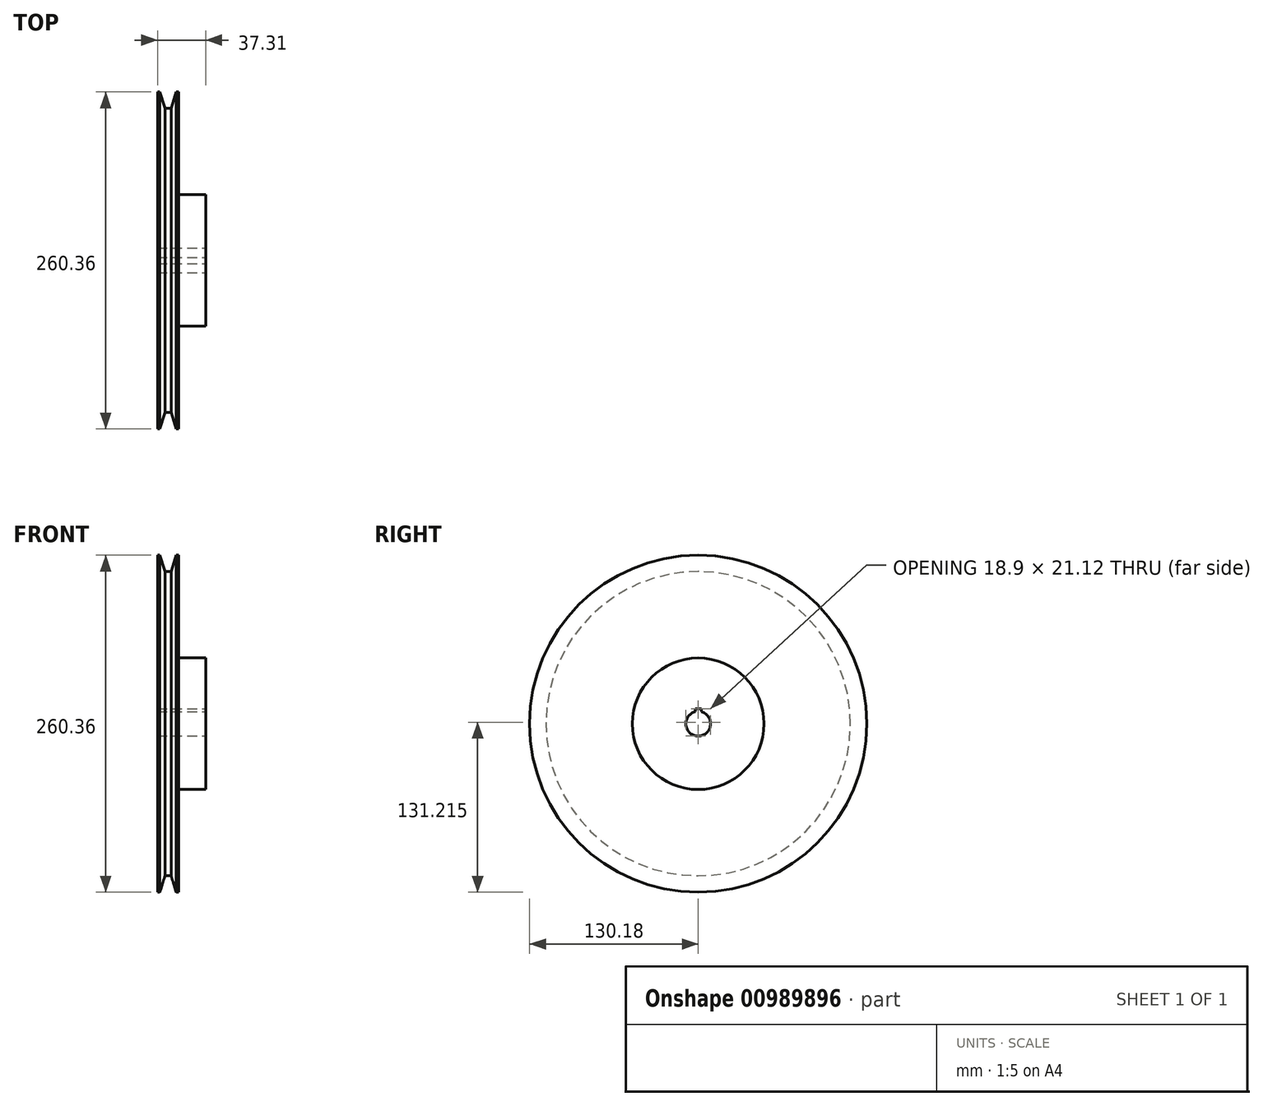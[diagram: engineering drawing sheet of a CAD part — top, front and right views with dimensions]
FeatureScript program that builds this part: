
annotation { "Feature Type Name" : "Feature", "Feature Type Description" : "" }
export const myFeature = defineFeature(function(context is Context, id is Id, definition is map)
    precondition{}
    {
        {
            var Q0;
            Q0=qCreatedBy(makeId("Front.planeOp"),FACE);
            var sketch = newSketch(context, id + "F0", { "sketchPlane" : qUnion([Q0])});
            skLineSegment(sketch, "E0", {"start": v(8.14, 9.53) * mm, "end": v(-8.14, 9.53) * mm});
            skLineSegment(sketch, "E1", {"start": v(-8.14, 9.52) * mm, "end": v(-8.14, 130.18) * mm});
            skLineSegment(sketch, "E2", {"start": v(-6.27, 130.18) * mm, "end": v(-8.14, 130.18) * mm});
            skLineSegment(sketch, "E3", {"start": v(-6.27, 130.18) * mm, "end": v(-2.4, 117.48) * mm});
            skLineSegment(sketch, "E4", {"start": v(-2.4, 117.48) * mm, "end": v(2.4, 117.48) * mm});
            skLineSegment(sketch, "E5", {"start": v(2.4, 117.48) * mm, "end": v(6.27, 130.18) * mm});
            skLineSegment(sketch, "E6", {"start": v(6.27, 130.18) * mm, "end": v(8.14, 130.18) * mm});
            skLineSegment(sketch, "E7", {"start": v(8.14, 130.18) * mm, "end": v(8.14, 50.8) * mm});
            skLineSegment(sketch, "E8", {"start": v(0, 117.48) * mm, "end": v(0, 0) * mm, "construction": true});
            skPoint(sketch, "E9", {"position": v(0, 9.53) * mm});
            skLineSegment(sketch, "E10", {"start": v(0, 0) * mm, "end": v(-51.93, 0) * mm, "construction": true});
            skLineSegment(sketch, "E11.bottom", {"start": v(8.14, 9.53) * mm, "end": v(29.17, 9.53) * mm});
            skLineSegment(sketch, "E11.top", {"start": v(8.14, 50.8) * mm, "end": v(29.17, 50.8) * mm});
            skLineSegment(sketch, "E11.right", {"start": v(29.17, 9.53) * mm, "end": v(29.17, 50.8) * mm});
            skSolve(sketch);
        }
        {
            var Q0;
            Q0=qSketchRegion(id+"F0",true);
            var Q1;
            Q1=sQuery(id+"F0.wireOp",EDGE,"E10");
            revolve(context, id + "F1", {"surfaceOperationType" : NewSurfaceOperationType.NEW, "entities" : qUnion([Q0]), "axis" : qUnion([Q1]), "revolveType" : RevolveType.FULL});
        }
        {
            var Q0;
            Q0=qCreatedBy(makeId("Right.planeOp"),FACE);
            var sketch = newSketch(context, id + "F2", { "sketchPlane" : qUnion([Q0])});
            skLineSegment(sketch, "E12.bottom", {"start": v(-2.38, 11.6) * mm, "end": v(2.38, 11.6) * mm});
            skLineSegment(sketch, "E12.left", {"start": v(-2.38, 11.6) * mm, "end": v(-2.38, 9.22) * mm});
            skLineSegment(sketch, "E12.right", {"start": v(2.38, 11.6) * mm, "end": v(2.38, 9.22) * mm});
            skArc(sketch, "E13.0", {"start": v(-2.38, 9.22) * mm, "mid": v(0, -9.53) * mm, "end": v(2.38, 9.22) * mm});
            skLineSegment(sketch, "E14", {"start": v(0, 0) * mm, "end": v(0, 11.6) * mm, "construction": true});
            skCircle(sketch, "E15", {"center": v(0, 0) * mm, "radius": 9.53 * mm, "construction": true});
            skPoint(sketch, "E16", {"position": v(0, 9.53) * mm});
            skLineSegment(sketch, "E17", {"start": v(-2.38, 6.83) * mm, "end": v(2.38, 6.83) * mm, "construction": true});
            skSolve(sketch);
        }
        {
            var Q0;
            Q0=qSketchRegion(id+"F2",true);
            extrude(context, id + "F3", {"entities" : qUnion([Q0]), "operationType" : NewBodyOperationType.REMOVE, "endBound" : BoundingType.THROUGH_ALL, "oppositeDirection" : true, "depth" : 25.4 * mm, "offsetDistance" : 25.4 * mm, "hasSecondDirection" : true, "secondDirectionBound" : SecondDirectionBoundingType.THROUGH_ALL, "secondDirectionOppositeDirection" : false, "secondDirectionDepth" : 25.4 * mm});
        }
    });
